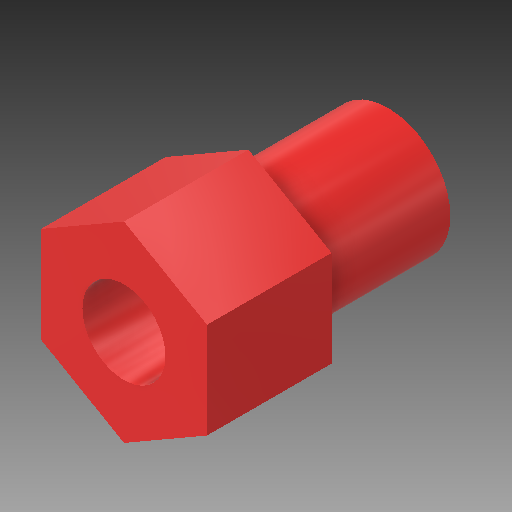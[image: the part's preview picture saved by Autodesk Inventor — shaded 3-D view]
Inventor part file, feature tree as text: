
AUTODESK INVENTOR PART (.ipt)
format: ipt  version: 2017 SP1 (Build 210196100, 196)  size: 130,560 bytes
history: native  units: in
note: dims shown in document units (in); Inventor stores cm internally (conversion verified against a paired STEP export)
features: extrude x2, sketch x2
ambient origin geometry x8: Origin, YZ Plane, XZ Plane, XY Plane, X Axis, Y Axis, Z Axis, Center Point
bodies: Solid1 (feature_tree)
feature tree (4):
  extrude  "Extrusion1"  Depth=0.375in
  extrude  "Extrusion2"  Depth=0.5in
  sketch  "Sketch1"  dims[d0=0.25in d1=0.375in]
  sketch  "Sketch2"  dims[d2=0.42in d3=0.0in d4=0.5in d5=0.375in d6=0.0in]
